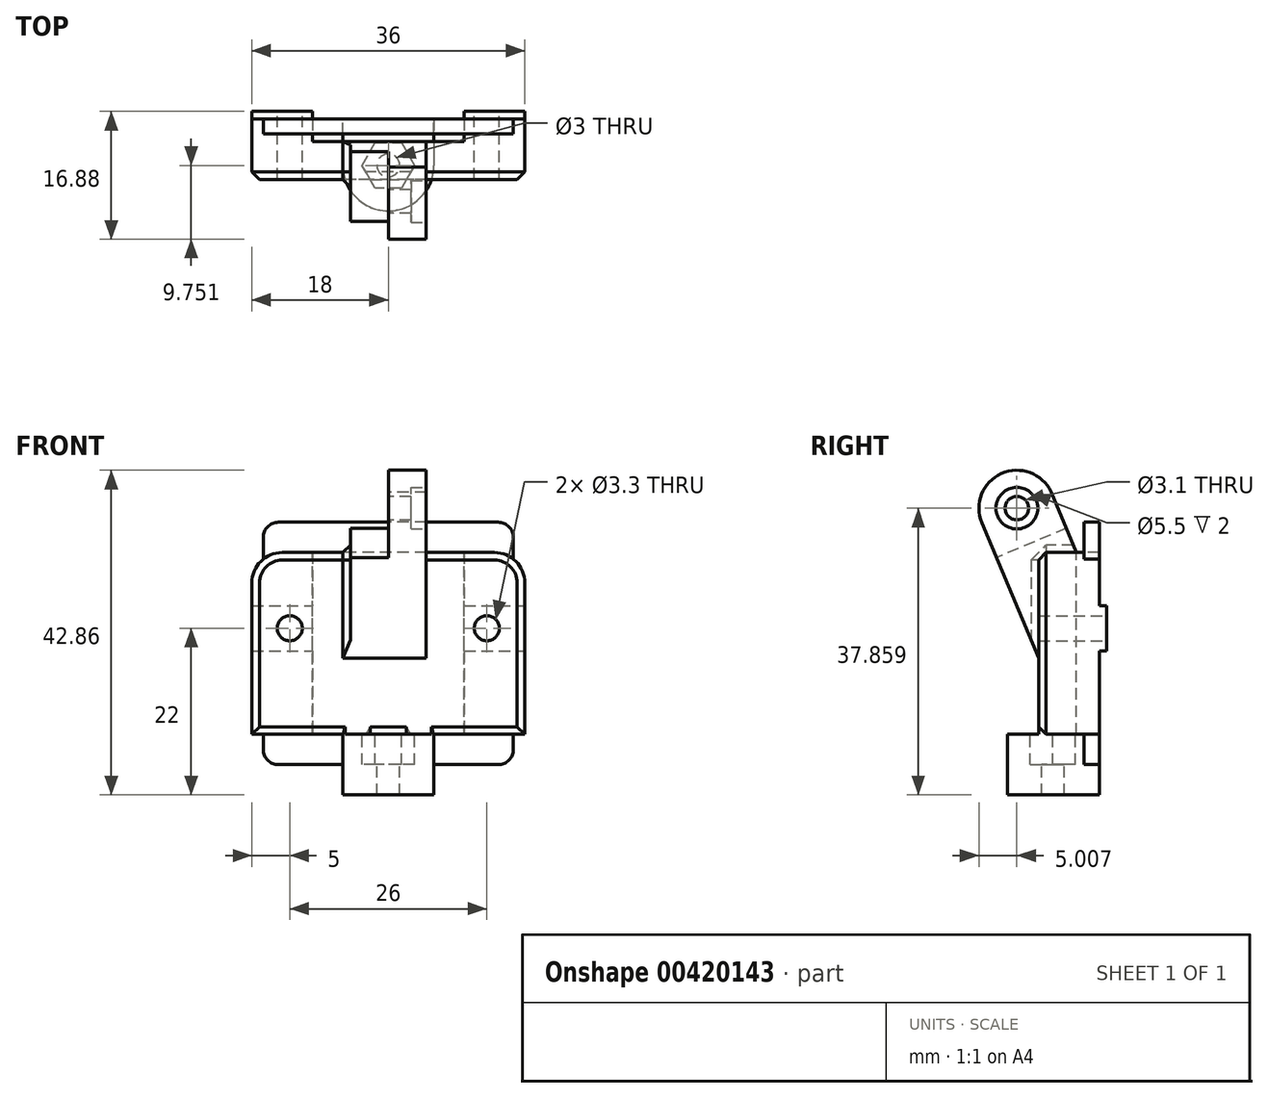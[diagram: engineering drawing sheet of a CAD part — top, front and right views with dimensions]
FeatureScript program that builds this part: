
annotation { "Feature Type Name" : "Feature", "Feature Type Description" : "" }
export const myFeature = defineFeature(function(context is Context, id is Id, definition is map)
    precondition{}
    {
        {
            var Q0;
            Q0=qCreatedBy(makeId("Front.planeOp"),FACE);
            var sketch = newSketch(context, id + "F0", { "sketchPlane" : qUnion([Q0])});
            skLineSegment(sketch, "E0.bottom", {"start": v(12.5, -12) * mm, "end": v(-12.5, -12) * mm, "construction": true});
            skLineSegment(sketch, "E0.top", {"start": v(12.5, 12) * mm, "end": v(-12.5, 12) * mm, "construction": true});
            skLineSegment(sketch, "E0.left", {"start": v(12.5, -12) * mm, "end": v(12.5, 12) * mm, "construction": true});
            skLineSegment(sketch, "E0.right", {"start": v(-12.5, -12) * mm, "end": v(-12.5, 12) * mm, "construction": true});
            skPoint(sketch, "E0.middle", {"position": v(0, 0) * mm});
            skLineSegment(sketch, "E1.bottom", {"start": v(16.5, -16) * mm, "end": v(-16.5, -16) * mm});
            skLineSegment(sketch, "E1.top", {"start": v(16.5, 16) * mm, "end": v(-16.5, 16) * mm});
            skLineSegment(sketch, "E1.left", {"start": v(16.5, -16) * mm, "end": v(16.5, 16) * mm});
            skLineSegment(sketch, "E1.right", {"start": v(-16.5, -16) * mm, "end": v(-16.5, 16) * mm});
            skSolve(sketch);
        }
        {
            var Q0;
            Q0 = qSketchRegion(id + "F0", true);
            extrude(context, id + "F1", {"entities" : qUnion([Q0]), "depth" : 2 * mm});
        }
        {
            var Q0;
            Q0=makeQuery(id+"F1.opExtrude","SWEPT_FACE",FACE,{"disambiguationData":[OSD([sQuery(id+"F0.wireOp",EDGE,"E1.bottom")])]});
            var sketch = newSketch(context, id + "F2", { "sketchPlane" : qUnion([Q0])});
            skLineSegment(sketch, "E2", {"start": v(0, 0) * mm, "end": v(0, 10.59) * mm, "construction": true});
            skPoint(sketch, "E2.endSnap0", {"position": v(0, 2) * mm});
            skLineSegment(sketch, "E3", {"start": v(-6, 0) * mm, "end": v(-6, 6.13) * mm});
            skArc(sketch, "E4", {"start": v(-6, 6.13) * mm, "mid": v(-4.24, 10.37) * mm, "end": v(0, 12.13) * mm});
            skLineSegment(sketch, "E5", {"start": v(0, 6.13) * mm, "end": v(-6, 6.13) * mm, "construction": true});
            skArc(sketch, "E6.MirrorCS", {"start": v(6, 6.13) * mm, "mid": v(4.24, 10.37) * mm, "end": v(0, 12.13) * mm});
            skLineSegment(sketch, "E7.MirrorCS", {"start": v(6, 0) * mm, "end": v(6, 6.13) * mm});
            skLineSegment(sketch, "E8", {"start": v(-6, 0) * mm, "end": v(6, 0) * mm});
            skCircle(sketch, "E9", {"center": v(0, 6.13) * mm, "radius": 1.5 * mm});
            skSolve(sketch);
        }
        {
            var Q0;
            Q0 = qSketchRegion(id + "F2", true);
            extrude(context, id + "F3", {"entities" : qUnion([Q0]), "operationType" : NewBodyOperationType.ADD, "depth" : 4 * mm, "hasSecondDirection" : true, "secondDirectionOppositeDirection" : true, "secondDirectionDepth" : 4 * mm});
        }
        {
            var Q0;
            Q0=makeQuery(id+"F3.opExtrude","CAP_FACE",FACE,{"disambiguationData":[OSD([sQuery(id+"F2.wireOp",EDGE,"E3"),sQuery(id+"F2.wireOp",EDGE,"E4"),sQuery(id+"F2.wireOp",EDGE,"E6.MirrorCS"),sQuery(id+"F2.wireOp",EDGE,"E7.MirrorCS"),sQuery(id+"F2.wireOp",EDGE,"E8"),sQuery(id+"F2.wireOp",EDGE,"E9")])],"isStart":true});
            var sketch = newSketch(context, id + "F4", { "sketchPlane" : qUnion([Q0])});
            skCircle(sketch, "E10.cCircle", {"center": v(0, -6.13) * mm, "radius": 3 * mm, "construction": true});
            skLineSegment(sketch, "E10.0", {"start": v(-1.73, -9.13) * mm, "end": v(-3.46, -6.13) * mm});
            skLineSegment(sketch, "E10.1", {"start": v(-3.46, -6.13) * mm, "end": v(-1.73, -3.13) * mm});
            skLineSegment(sketch, "E10.2", {"start": v(-1.73, -3.13) * mm, "end": v(1.73, -3.13) * mm});
            skLineSegment(sketch, "E10.3", {"start": v(1.73, -3.13) * mm, "end": v(3.46, -6.13) * mm});
            skLineSegment(sketch, "E10.4", {"start": v(3.46, -6.13) * mm, "end": v(1.73, -9.13) * mm});
            skLineSegment(sketch, "E10.5", {"start": v(1.73, -9.13) * mm, "end": v(-1.73, -9.13) * mm});
            skPoint(sketch, "E10.0.midPoint", {"position": v(-2.6, -7.63) * mm});
            skSolve(sketch);
        }
        {
            var Q0;
            Q0 = qSketchRegion(id + "F4", true);
            extrude(context, id + "F5", {"entities" : qUnion([Q0]), "operationType" : NewBodyOperationType.REMOVE, "oppositeDirection" : true, "depth" : 4 * mm});
        }
        {
            var Q0;
            Q0=makeQuery(id+"F3.boolean.opBoolean","MERGE",FACE,{"derivedFrom":[makeQuery(id+"F1.opExtrude","CAP_FACE",FACE,{"disambiguationData":[OSD([sQuery(id+"F0.wireOp",EDGE,"E1.bottom"),sQuery(id+"F0.wireOp",EDGE,"E1.top"),sQuery(id+"F0.wireOp",EDGE,"E1.left"),sQuery(id+"F0.wireOp",EDGE,"E1.right")])],"isStart":true}),makeQuery(id+"F3.opExtrude","SWEPT_FACE",FACE,{"disambiguationData":[OSD([sQuery(id+"F2.wireOp",EDGE,"E8")])]})]});
            var sketch = newSketch(context, id + "F6", { "sketchPlane" : qUnion([Q0])});
            skLineSegment(sketch, "E11.bottom", {"start": v(-10.5, 4) * mm, "end": v(10.5, 4) * mm, "construction": true});
            skLineSegment(sketch, "E11.top", {"start": v(-10.5, -10) * mm, "end": v(10.5, -10) * mm, "construction": true});
            skLineSegment(sketch, "E11.left", {"start": v(-10.5, 4) * mm, "end": v(-10.5, -10) * mm, "construction": true});
            skLineSegment(sketch, "E11.right", {"start": v(10.5, 4) * mm, "end": v(10.5, -10) * mm, "construction": true});
            skPoint(sketch, "E11.middle", {"position": v(0, -3) * mm});
            skCircle(sketch, "E12", {"center": v(10.5, -10) * mm, "radius": 1.25 * mm});
            skCircle(sketch, "E13", {"center": v(10.5, 4) * mm, "radius": 1.25 * mm});
            skCircle(sketch, "E14", {"center": v(-10.5, 4) * mm, "radius": 1.25 * mm});
            skCircle(sketch, "E15", {"center": v(-10.5, -10) * mm, "radius": 1.25 * mm});
            skSolve(sketch);
        }
        {
            var Q0;
            Q0 = qSketchRegion(id + "F6", true);
            extrude(context, id + "F7", {"entities" : qUnion([Q0]), "operationType" : NewBodyOperationType.REMOVE, "endBound" : BoundingType.UP_TO_NEXT, "oppositeDirection" : true, "depth" : 25 * mm});
        }
        {
            var Q0;
            Q0=makeQuery(id+"F1.opExtrude","SWEPT_EDGE",EDGE,{"disambiguationData":[OSD([sQuery(id+"F0.wireOp",EDGE,"E1.bottom"),sQuery(id+"F0.wireOp",EDGE,"E1.right")])]});
            var Q1;
            Q1=makeQuery(id+"F1.opExtrude","SWEPT_EDGE",EDGE,{"disambiguationData":[OSD([sQuery(id+"F0.wireOp",EDGE,"E1.bottom"),sQuery(id+"F0.wireOp",EDGE,"E1.left")])]});
            var Q2;
            Q2=makeQuery(id+"F1.opExtrude","SWEPT_EDGE",EDGE,{"disambiguationData":[OSD([sQuery(id+"F0.wireOp",EDGE,"E1.top"),sQuery(id+"F0.wireOp",EDGE,"E1.left")])]});
            var Q3;
            Q3=makeQuery(id+"F1.opExtrude","SWEPT_EDGE",EDGE,{"disambiguationData":[OSD([sQuery(id+"F0.wireOp",EDGE,"E1.top"),sQuery(id+"F0.wireOp",EDGE,"E1.right")])]});
            fillet(context, id + "F8", {"entities" : qUnion([Q0, Q1, Q2, Q3]), "radius" : 2 * mm, "tangentPropagation" : true, "allowEdgeOverflow" : false});
        }
        {
            var Q0;
            Q0=qCreatedBy(makeId("Front.planeOp"),FACE);
            var sketch = newSketch(context, id + "F9", { "sketchPlane" : qUnion([Q0])});
            skLineSegment(sketch, "E16.bottom", {"start": v(18, -12) * mm, "end": v(-18, -12) * mm});
            skLineSegment(sketch, "E16.top", {"start": v(14, 12) * mm, "end": v(-14, 12) * mm});
            skLineSegment(sketch, "E16.left", {"start": v(18, -12) * mm, "end": v(18, 8) * mm});
            skLineSegment(sketch, "E16.right", {"start": v(-18, -12) * mm, "end": v(-18, 8) * mm});
            skPoint(sketch, "E16.middle", {"position": v(0, 0) * mm});
            skPoint(sketch, "E17.visualSharp", {"position": v(-18, 12) * mm});
            skArc(sketch, "E17.filletArc", {"start": v(-14, 12) * mm, "mid": v(-16.83, 10.83) * mm, "end": v(-18, 8) * mm});
            skPoint(sketch, "E18.visualSharp", {"position": v(18, 12) * mm});
            skArc(sketch, "E18.filletArc", {"start": v(18, 8) * mm, "mid": v(16.83, 10.83) * mm, "end": v(14, 12) * mm});
            skSolve(sketch);
        }
        {
            var Q0;
            Q0 = qSketchRegion(id + "F9", true);
            extrude(context, id + "F10", {"entities" : qUnion([Q0]), "depth" : 8 * mm});
        }
        {
            var Q0;
            Q0=makeQuery(id+"F10.opExtrude","CAP_FACE",FACE,{"disambiguationData":[OSD([sQuery(id+"F9.wireOp",EDGE,"E16.bottom"),sQuery(id+"F9.wireOp",EDGE,"E16.top"),sQuery(id+"F9.wireOp",EDGE,"E16.left"),sQuery(id+"F9.wireOp",EDGE,"E16.right"),sQuery(id+"F9.wireOp",EDGE,"E17.filletArc"),sQuery(id+"F9.wireOp",EDGE,"E18.filletArc")])],"isStart":true});
            var sketch = newSketch(context, id + "F11", { "sketchPlane" : qUnion([Q0])});
            skLineSegment(sketch, "E19.bottom", {"start": v(18, -1) * mm, "end": v(-18, -1) * mm});
            skLineSegment(sketch, "E19.top", {"start": v(18, 5) * mm, "end": v(-18, 5) * mm});
            skLineSegment(sketch, "E19.left", {"start": v(18, -1) * mm, "end": v(18, 5) * mm});
            skLineSegment(sketch, "E19.right", {"start": v(-18, -1) * mm, "end": v(-18, 5) * mm});
            skPoint(sketch, "E19.middle", {"position": v(0, 2) * mm});
            skLineSegment(sketch, "E20.0", {"start": v(-14, 12) * mm, "end": v(14, 12) * mm, "construction": true});
            skSolve(sketch);
        }
        {
            var Q0;
            Q0 = qSketchRegion(id + "F11", true);
            extrude(context, id + "F12", {"entities" : qUnion([Q0]), "operationType" : NewBodyOperationType.ADD, "depth" : 1 * mm});
        }
        {
            var Q0;
            Q0=makeQuery(id+"F12.opExtrude","CAP_FACE",FACE,{"disambiguationData":[OSD([sQuery(id+"F11.wireOp",EDGE,"E19.bottom"),sQuery(id+"F11.wireOp",EDGE,"E19.top"),sQuery(id+"F11.wireOp",EDGE,"E19.left"),sQuery(id+"F11.wireOp",EDGE,"E19.right")])],"isStart":false});
            var sketch = newSketch(context, id + "F13", { "sketchPlane" : qUnion([Q0])});
            skLineSegment(sketch, "E21.0", {"start": v(-18, -1) * mm, "end": v(-18, 5) * mm, "construction": true});
            skLineSegment(sketch, "E21.1", {"start": v(18, 5) * mm, "end": v(-18, 5) * mm, "construction": true});
            skLineSegment(sketch, "E21.2", {"start": v(18, -1) * mm, "end": v(-18, -1) * mm, "construction": true});
            skLineSegment(sketch, "E21.3", {"start": v(18, -1) * mm, "end": v(18, 5) * mm, "construction": true});
            skLineSegment(sketch, "E22", {"start": v(-18, 2) * mm, "end": v(18, 2) * mm, "construction": true});
            skLineSegment(sketch, "E23", {"start": v(0, 5) * mm, "end": v(0, -1) * mm, "construction": true});
            skCircle(sketch, "E24", {"center": v(-13, 2) * mm, "radius": 1.65 * mm});
            skCircle(sketch, "E25.MirrorC", {"center": v(13, 2) * mm, "radius": 1.65 * mm});
            skSolve(sketch);
        }
        {
            var Q0;
            Q0 = qSketchRegion(id + "F13", true);
            var Q1;
            Q1=makeQuery(id+"F10.opExtrude","CAP_FACE",FACE,{"disambiguationData":[OSD([sQuery(id+"F9.wireOp",EDGE,"E16.bottom"),sQuery(id+"F9.wireOp",EDGE,"E16.top"),sQuery(id+"F9.wireOp",EDGE,"E16.left"),sQuery(id+"F9.wireOp",EDGE,"E16.right"),sQuery(id+"F9.wireOp",EDGE,"E17.filletArc"),sQuery(id+"F9.wireOp",EDGE,"E18.filletArc")])],"isStart":false});
            extrude(context, id + "F14", {"entities" : qUnion([Q0]), "operationType" : NewBodyOperationType.REMOVE, "endBound" : BoundingType.UP_TO_SURFACE, "oppositeDirection" : true, "endBoundEntityFace" : qUnion([Q1]), "depth" : 25 * mm});
        }
        {
            var Q0;
            Q0=makeQuery(id+"F10.opExtrude","SWEPT_FACE",FACE,{"disambiguationData":[OSD([sQuery(id+"F9.wireOp",EDGE,"E16.top")])]});
            var sketch = newSketch(context, id + "F15", { "sketchPlane" : qUnion([Q0])});
            skLineSegment(sketch, "E26.0", {"start": v(-18, 1) * mm, "end": v(18, 1) * mm, "construction": true});
            skLineSegment(sketch, "E27", {"start": v(0, 1) * mm, "end": v(0, -8) * mm, "construction": true});
            skLineSegment(sketch, "E28", {"start": v(0, 1) * mm, "end": v(-10, 1) * mm});
            skLineSegment(sketch, "E29", {"start": v(-10, 1) * mm, "end": v(-10, -3) * mm});
            skLineSegment(sketch, "E30", {"start": v(-10, -3) * mm, "end": v(0, -3) * mm});
            skLineSegment(sketch, "E31.MirrorCS", {"start": v(0, 1) * mm, "end": v(10, 1) * mm});
            skLineSegment(sketch, "E32.MirrorCS", {"start": v(10, -3) * mm, "end": v(0, -3) * mm});
            skLineSegment(sketch, "E33.MirrorCS", {"start": v(10, 1) * mm, "end": v(10, -3) * mm});
            skSolve(sketch);
        }
        {
            var Q0;
            Q0 = qSketchRegion(id + "F15", true);
            var Q1;
            Q1=makeQuery(id+"F10.opExtrude","SWEPT_FACE",FACE,{"disambiguationData":[OSD([sQuery(id+"F9.wireOp",EDGE,"E16.bottom")])]});
            extrude(context, id + "F16", {"entities" : qUnion([Q0]), "operationType" : NewBodyOperationType.REMOVE, "endBound" : BoundingType.UP_TO_SURFACE, "oppositeDirection" : true, "endBoundEntityFace" : qUnion([Q1]), "depth" : 25 * mm});
        }
        {
            var Q0;
            Q0=qCreatedBy(makeId("Right.planeOp"),FACE);
            var sketch = newSketch(context, id + "F17", { "sketchPlane" : qUnion([Q0])});
            skLineSegment(sketch, "E34.0", {"start": v(-8, 12) * mm, "end": v(-3, 12) * mm, "construction": true});
            skLineSegment(sketch, "E34.1", {"start": v(-8, 12) * mm, "end": v(-8, -1.94) * mm, "construction": true});
            skLineSegment(sketch, "E35", {"start": v(-8, -1.94) * mm, "end": v(-15.49, 15.93) * mm});
            skLineSegment(sketch, "E36", {"start": v(-3, 12) * mm, "end": v(-6.35, 20) * mm});
            skArc(sketch, "E37", {"start": v(-6.35, 20) * mm, "mid": v(-12.9, 22.43) * mm, "end": v(-15.49, 15.93) * mm});
            skLineSegment(sketch, "E38", {"start": v(-3, 12) * mm, "end": v(-8, 12) * mm});
            skLineSegment(sketch, "E39", {"start": v(-8, -1.94) * mm, "end": v(-8, 12) * mm});
            skSolve(sketch);
        }
        {
            var Q0;
            Q0 = qSketchRegion(id + "F17", true);
            extrude(context, id + "F18", {"entities" : qUnion([Q0]), "operationType" : NewBodyOperationType.ADD, "depth" : 5 * mm, "hasSecondDirection" : true, "secondDirectionOppositeDirection" : true, "secondDirectionDepth" : 5 * mm});
        }
        {
            var Q0;
            Q0=makeQuery(id+"F18.opExtrude","CAP_FACE",FACE,{"disambiguationData":[OSD([sQuery(id+"F17.wireOp",EDGE,"E35"),sQuery(id+"F17.wireOp",EDGE,"E36"),sQuery(id+"F17.wireOp",EDGE,"E37"),sQuery(id+"F17.wireOp",EDGE,"E38"),sQuery(id+"F17.wireOp",EDGE,"E39")])],"isStart":true});
            var sketch = newSketch(context, id + "F19", { "sketchPlane" : qUnion([Q0])});
            skArc(sketch, "E40.0", {"start": v(6.35, 20) * mm, "mid": v(12.9, 22.43) * mm, "end": v(15.49, 15.93) * mm});
            skLineSegment(sketch, "E41.0", {"start": v(3.84, 14) * mm, "end": v(6.35, 20) * mm, "construction": true});
            skLineSegment(sketch, "E41.1", {"start": v(10, 2.83) * mm, "end": v(15.49, 15.93) * mm, "construction": true});
            skLineSegment(sketch, "E42", {"start": v(6.35, 20) * mm, "end": v(4.33, 15.18) * mm});
            skLineSegment(sketch, "E43", {"start": v(4.33, 15.18) * mm, "end": v(13.56, 11.32) * mm});
            skLineSegment(sketch, "E44", {"start": v(13.56, 11.32) * mm, "end": v(15.49, 15.93) * mm});
            skSolve(sketch);
        }
        {
            var Q0;
            Q0 = qSketchRegion(id + "F19", true);
            extrude(context, id + "F20", {"entities" : qUnion([Q0]), "operationType" : NewBodyOperationType.REMOVE, "oppositeDirection" : true, "depth" : 5 * mm});
        }
        {
            var Q0;
            Q0=makeQuery(id+"F18.opExtrude","CAP_EDGE",EDGE,{"disambiguationData":[OSD([sQuery(id+"F17.wireOp",EDGE,"E39")])],"isStart":true});
            var Q1;
            Q1=makeQuery(id+"F18.opExtrude","CAP_EDGE",EDGE,{"disambiguationData":[OSD([sQuery(id+"F17.wireOp",EDGE,"E38")])],"isStart":true});
            var Q2;
            Q2=makeQuery(id+"F18.opExtrude","CAP_EDGE",EDGE,{"disambiguationData":[OSD([sQuery(id+"F17.wireOp",EDGE,"E39")])],"isStart":false});
            var Q3;
            Q3=makeQuery(id+"F18.opExtrude","CAP_EDGE",EDGE,{"disambiguationData":[OSD([sQuery(id+"F17.wireOp",EDGE,"E38")])],"isStart":false});
            var Q4;
            {var subQ0=sQuery(id+"F9.wireOp",EDGE,"E17.filletArc");var subQ1=sQuery(id+"F9.wireOp",EDGE,"E16.top");Q4=makeQuery(id+"F18.boolean.opBoolean","SPLIT",EDGE,{"disambiguationData":[TD([makeQuery(id+"F10.opExtrude","SWEPT_FACE",FACE,{"disambiguationData":[OSD([subQ0])]})])],"derivedFrom":makeQuery(id+"F10.opExtrude","CAP_EDGE",EDGE,{"disambiguationData":[OSD([subQ1])],"isStart":false})});}
            var Q5;
            Q5=makeQuery(id+"F10.opExtrude","CAP_EDGE",EDGE,{"disambiguationData":[OSD([sQuery(id+"F9.wireOp",EDGE,"E17.filletArc")])],"isStart":false});
            var Q6;
            Q6=makeQuery(id+"F10.opExtrude","CAP_EDGE",EDGE,{"disambiguationData":[OSD([sQuery(id+"F9.wireOp",EDGE,"E16.right")])],"isStart":false});
            var Q7;
            {var subQ0=sQuery(id+"F9.wireOp",EDGE,"E18.filletArc");var subQ1=sQuery(id+"F9.wireOp",EDGE,"E16.top");Q7=makeQuery(id+"F18.boolean.opBoolean","SPLIT",EDGE,{"disambiguationData":[TD([makeQuery(id+"F10.opExtrude","SWEPT_FACE",FACE,{"disambiguationData":[OSD([subQ0])]})])],"derivedFrom":makeQuery(id+"F10.opExtrude","CAP_EDGE",EDGE,{"disambiguationData":[OSD([subQ1])],"isStart":false})});}
            var Q8;
            Q8=makeQuery(id+"F10.opExtrude","CAP_EDGE",EDGE,{"disambiguationData":[OSD([sQuery(id+"F9.wireOp",EDGE,"E18.filletArc")])],"isStart":false});
            var Q9;
            Q9=makeQuery(id+"F10.opExtrude","CAP_EDGE",EDGE,{"disambiguationData":[OSD([sQuery(id+"F9.wireOp",EDGE,"E16.bottom")])],"isStart":false});
            chamfer(context, id + "F21", {"entities" : qUnion([Q0, Q1, Q2, Q3, Q4, Q5, Q6, Q7, Q8, Q9]), "width" : 1 * mm, "tangentPropagation" : true});
        }
        {
            var Q0;
            Q0=makeQuery(id+"F20.boolean.opBoolean","COPY",FACE,{"derivedFrom":makeQuery(id+"F20.opExtrude","CAP_FACE",FACE,{"disambiguationData":[OSD([sQuery(id+"F19.wireOp",EDGE,"E40.0"),sQuery(id+"F19.wireOp",EDGE,"E42"),sQuery(id+"F19.wireOp",EDGE,"E43"),sQuery(id+"F19.wireOp",EDGE,"E44")])],"isStart":false})});
            var sketch = newSketch(context, id + "F22", { "sketchPlane" : qUnion([Q0])});
            skArc(sketch, "E45.0", {"start": v(6.35, 20) * mm, "mid": v(12.9, 22.43) * mm, "end": v(15.49, 15.93) * mm, "construction": true});
            skCircle(sketch, "E46", {"center": v(10.87, 17.86) * mm, "radius": 1.55 * mm});
            skSolve(sketch);
        }
        {
            var Q0;
            Q0 = qSketchRegion(id + "F22", true);
            var Q1;
            Q1=makeQuery(id+"F18.opExtrude","CAP_FACE",FACE,{"disambiguationData":[OSD([sQuery(id+"F17.wireOp",EDGE,"E35"),sQuery(id+"F17.wireOp",EDGE,"E36"),sQuery(id+"F17.wireOp",EDGE,"E37"),sQuery(id+"F17.wireOp",EDGE,"E38"),sQuery(id+"F17.wireOp",EDGE,"E39")])],"isStart":false});
            extrude(context, id + "F23", {"entities" : qUnion([Q0]), "operationType" : NewBodyOperationType.REMOVE, "endBound" : BoundingType.UP_TO_SURFACE, "oppositeDirection" : true, "endBoundEntityFace" : qUnion([Q1]), "depth" : 25 * mm});
        }
        {
            var Q0;
            Q0=makeQuery(id+"F18.opExtrude","CAP_FACE",FACE,{"disambiguationData":[OSD([sQuery(id+"F17.wireOp",EDGE,"E35"),sQuery(id+"F17.wireOp",EDGE,"E36"),sQuery(id+"F17.wireOp",EDGE,"E37"),sQuery(id+"F17.wireOp",EDGE,"E38"),sQuery(id+"F17.wireOp",EDGE,"E39")])],"isStart":false});
            var sketch = newSketch(context, id + "F24", { "sketchPlane" : qUnion([Q0])});
            skCircle(sketch, "E47.0", {"center": v(-10.87, 17.86) * mm, "radius": 1.55 * mm, "construction": true});
            skCircle(sketch, "E48", {"center": v(-10.87, 17.86) * mm, "radius": 2.75 * mm});
            skSolve(sketch);
        }
        {
            var Q0;
            Q0 = qSketchRegion(id + "F24", true);
            extrude(context, id + "F25", {"entities" : qUnion([Q0]), "operationType" : NewBodyOperationType.REMOVE, "oppositeDirection" : true, "depth" : 2 * mm});
        }
    });
